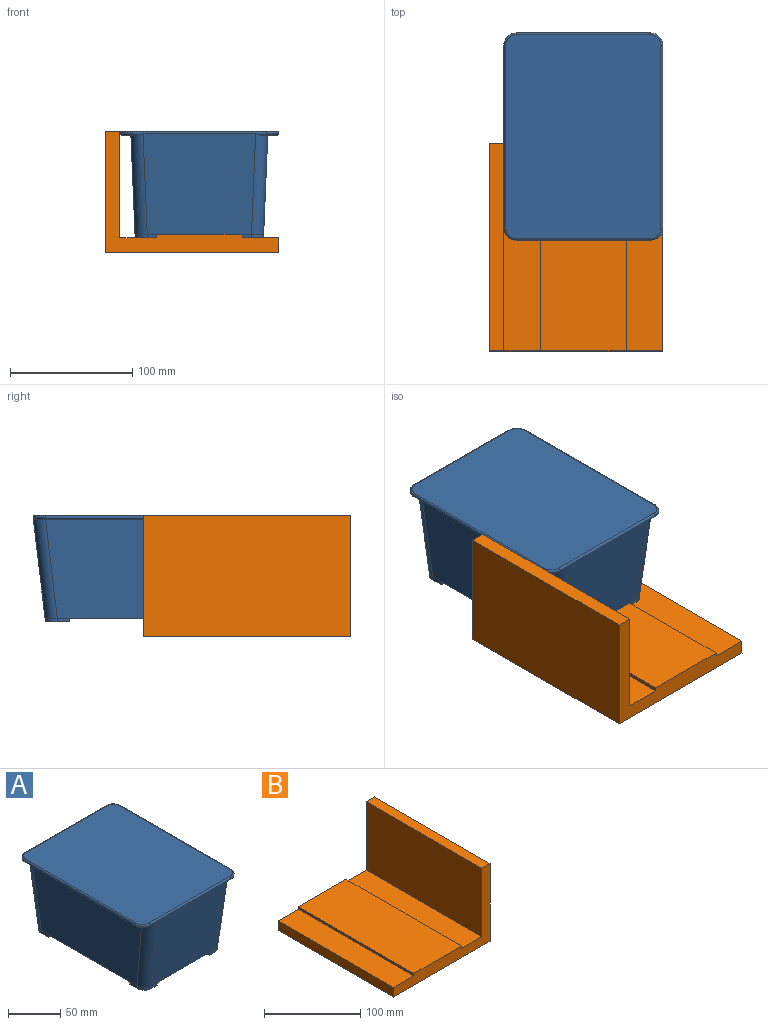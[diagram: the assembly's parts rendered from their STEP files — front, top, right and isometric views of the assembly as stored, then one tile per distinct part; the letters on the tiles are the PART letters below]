
ASSEMBLY  parts=2 mates=1
PART A: 48 faces, bbox 130x170x87 mm
  f0: plane 150x105.25mm, normal (0,0,-1), area 14377.5mm2, adj f1,f2,f6,f7,f24,f25,f30,f31
  f1: plane 149.24x81mm, normal (-1,0,-0.04), area 11317.5mm2, adj f0,f5,f10,f11,f34,f38
  f2: plane 149.24x81mm, normal (1,0,-0.04), area 11317.5mm2, adj f0,f3,f8,f9,f26,f46
  f3: plane 166.62x12.49mm, normal (0,0,-1), area 1243.6mm2, adj f2,f8,f9,f12,f13,f15,f17,f21
  f4: plane 166.62x127mm, normal (0,0,1), area 21098.5mm2, adj f12,f14,f15,f16,f19,f20,f21,f22
  f5: plane 166.62x12.49mm, normal (0,0,-1), area 1243.6mm2, adj f1,f10,f11,f12,f18,f19,f21,f23
  f6: plane 92.19x82.32mm, normal (0,-0.99,-0.12), area 7358.7mm2, adj f0,f8,f10,f21,f28,f32
  f7: plane 92.19x82.32mm, normal (0,0.99,-0.12), area 7358.7mm2, adj f0,f9,f11,f12,f40,f44
  f8: cylinder r=10mm len=83.92mm, axis (-0.04,0.12,-0.99), area 1281mm2, adj f2,f3,f6,f21,f27
  f9: cylinder r=10mm len=83.92mm, axis (-0.04,-0.12,-0.99), area 1281mm2, adj f2,f3,f7,f12,f45
  f10: cylinder r=10mm len=83.92mm, axis (0.04,0.12,-0.99), area 1281mm2, adj f1,f5,f6,f21,f33
  f11: cylinder r=10mm len=83.92mm, axis (0.04,-0.12,-0.99), area 1281mm2, adj f1,f5,f7,f12,f39
  f12: cylinder r=1.5mm len=110mm, axis (1,0,0), area 306.2mm2, adj f3,f4,f5,f7,f9,f11,f13,f14
  f13: bspline ~11.8x10.01mm, area 33.3mm2, adj f3,f12,f14,f15
  f14: bspline ~10.05x10mm, area 36.9mm2, adj f4,f12,f13,f15
  f15: cylinder r=1.5mm len=149.5mm, axis (0,1,0), area 704.5mm2, adj f3,f4,f13,f14,f17,f20
  f16: bspline ~12x10.01mm, area 36.9mm2, adj f4,f12,f18,f19
  f17: bspline ~11.8x10.01mm, area 33.3mm2, adj f3,f15,f20,f21
  f18: bspline ~11.8x10.01mm, area 33.3mm2, adj f5,f12,f16,f19
  f19: cylinder r=1.5mm len=149.5mm, axis (0,-1,0), area 704.5mm2, adj f4,f5,f16,f18,f22,f23
  f20: bspline ~12x10.01mm, area 36.9mm2, adj f4,f15,f17,f21
  f21: cylinder r=1.5mm len=110mm, axis (1,0,0), area 306.2mm2, adj f3,f4,f5,f6,f8,f10,f17,f20
  f22: bspline ~12x10.01mm, area 36.9mm2, adj f4,f19,f21,f23
  f23: bspline ~11.8x10.01mm, area 33.3mm2, adj f5,f19,f21,f22
  f24: plane 20x3mm, normal (-1,0,0), area 60mm2, adj f0,f25,f28,f29
  f25: plane 17.63x3mm, normal (0,1,0), area 52.9mm2, adj f0,f24,f26,f29
  f26: plane 9.98x3mm, normal (1,0,0), area 29.9mm2, adj f2,f25,f27,f29
  f27: extruded ~10.02x9.96mm, area 47.1mm2, adj f8,f26,f28,f29
  f28: plane 7.67x3mm, normal (0,-1,0), area 23mm2, adj f6,f24,f27,f29
  f29: plane 20x17.63mm, normal (0,0,-1), area 331.1mm2, adj f24,f25,f26,f27,f28
  f30: plane 17.63x3mm, normal (0,1,0), area 52.9mm2, adj f0,f31,f34,f35
  f31: plane 20x3mm, normal (1,0,0), area 60mm2, adj f0,f30,f32,f35
  f32: plane 7.67x3mm, normal (0,-1,0), area 23mm2, adj f6,f31,f33,f35
  f33: extruded ~10.02x9.96mm, area 47.1mm2, adj f10,f32,f34,f35
  f34: plane 9.98x3mm, normal (-1,0,0), area 29.9mm2, adj f1,f30,f33,f35
  f35: plane 20x17.63mm, normal (0,0,-1), area 331.1mm2, adj f30,f31,f32,f33,f34
  f36: plane 20x3mm, normal (1,0,0), area 60mm2, adj f0,f37,f40,f41
  f37: plane 17.63x3mm, normal (0,-1,0), area 52.9mm2, adj f0,f36,f38,f41
  f38: plane 9.98x3mm, normal (-1,0,0), area 29.9mm2, adj f1,f37,f39,f41
  f39: extruded ~10.02x9.96mm, area 47.1mm2, adj f11,f38,f40,f41
  f40: plane 7.67x3mm, normal (0,1,0), area 23mm2, adj f7,f36,f39,f41
  f41: plane 20x17.63mm, normal (0,0,-1), area 331.1mm2, adj f36,f37,f38,f39,f40
  f42: plane 17.63x3mm, normal (0,-1,0), area 52.9mm2, adj f0,f43,f46,f47
  f43: plane 20x3mm, normal (-1,0,0), area 60mm2, adj f0,f42,f44,f47
  f44: plane 7.67x3mm, normal (0,1,0), area 23mm2, adj f7,f43,f45,f47
  f45: extruded ~10.02x9.96mm, area 47.1mm2, adj f9,f44,f46,f47
  f46: plane 9.98x3mm, normal (1,0,0), area 29.9mm2, adj f2,f42,f45,f47
  f47: plane 20x17.63mm, normal (0,0,-1), area 331.1mm2, adj f42,f43,f44,f45,f46
PART B: 12 faces, bbox 142x170x99 mm
  f0: plane 170x30mm, normal (0,0,1), area 5100mm2, adj f1,f9,f10,f11
  f1: plane 170x3mm, normal (1,0,0), area 510mm2, adj f0,f2,f10,f11
  f2: plane 170x70mm, normal (0,0,1), area 11900mm2, adj f1,f3,f10,f11
  f3: plane 170x3mm, normal (-1,0,0), area 510mm2, adj f2,f4,f10,f11
  f4: plane 170x30mm, normal (0,0,1), area 5100mm2, adj f3,f5,f10,f11
  f5: plane 170x12mm, normal (-1,0,0), area 2040mm2, adj f4,f6,f10,f11
  f6: plane 170x142mm, normal (0,0,-1), area 24140mm2, adj f5,f7,f10,f11
  f7: plane 170x99mm, normal (1,0,0), area 16830mm2, adj f6,f8,f10,f11
  f8: plane 170x12mm, normal (0,0,1), area 2040mm2, adj f7,f9,f10,f11
  f9: plane 170x87mm, normal (-1,0,0), area 14790mm2, adj f0,f8,f10,f11
  f10: plane 142x99mm, normal (0,-1,0), area 2958mm2, adj f0,f1,f2,f3,f4,f5,f6,f7
  f11: plane 142x99mm, normal (0,1,0), area 2958mm2, adj f0,f1,f2,f3,f4,f5,f6,f7
PLACE A t=(-126.34,156.23,117.84)mm
PLACE B rot(axis=(0,0,1),180deg) t=(3.66,-103.99,30.84)mm fixed
MATE slider B.f10 <-> A.f40  axis (0,1,0) through (-96.34,66.01,30.84)mm
